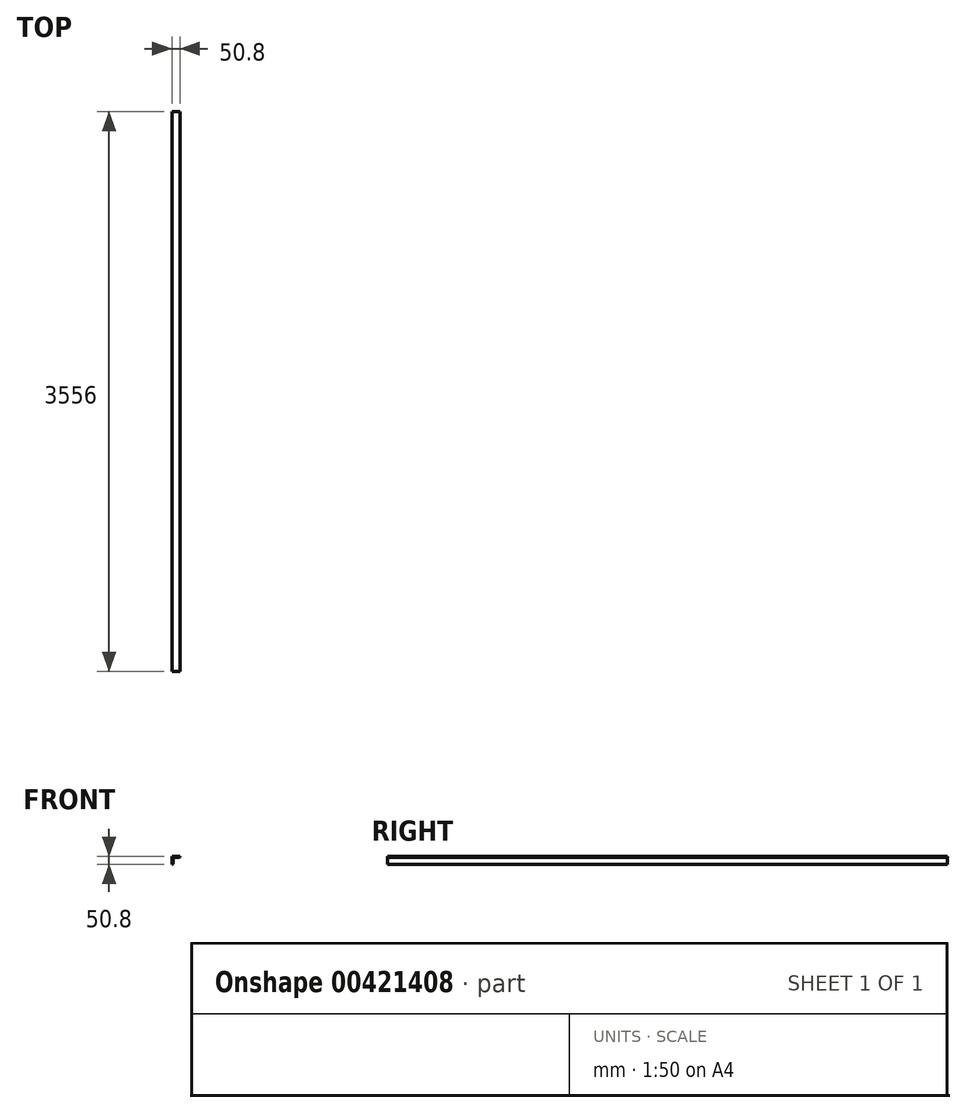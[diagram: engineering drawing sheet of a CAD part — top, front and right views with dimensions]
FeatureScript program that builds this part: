
annotation { "Feature Type Name" : "Feature", "Feature Type Description" : "" }
export const myFeature = defineFeature(function(context is Context, id is Id, definition is map)
    precondition{}
    {
        {
            var Q0;
            Q0=qCreatedBy(makeId("Front.planeOp"),FACE);
            var sketch = newSketch(context, id + "F0", { "sketchPlane" : qUnion([Q0])});
            skLineSegment(sketch, "E0", {"start": v(0, 0) * mm, "end": v(0, 50.8) * mm});
            skLineSegment(sketch, "E1", {"start": v(0, 50.8) * mm, "end": v(50.8, 50.8) * mm});
            skLineSegment(sketch, "E2", {"start": v(50.8, 50.8) * mm, "end": v(50.8, 44.45) * mm});
            skLineSegment(sketch, "E3", {"start": v(50.8, 44.45) * mm, "end": v(6.35, 44.45) * mm});
            skLineSegment(sketch, "E4", {"start": v(6.35, 44.45) * mm, "end": v(6.35, 0) * mm});
            skLineSegment(sketch, "E5", {"start": v(6.35, 0) * mm, "end": v(0, 0) * mm});
            skSolve(sketch);
        }
        {
            var Q0;
            Q0 = qSketchRegion(id + "F0", true);
            extrude(context, id + "F1", {"entities" : qUnion([Q0]), "depth" : 3556 * mm});
        }
        {
            var Q0;
            Q0=makeQuery(id+"F1.opExtrude","SWEPT_EDGE",EDGE,{"disambiguationData":[OSD([sQuery(id+"F0.wireOp",EDGE,"E4"),sQuery(id+"F0.wireOp",EDGE,"E5")])]});
            var Q1;
            Q1=makeQuery(id+"F1.opExtrude","SWEPT_EDGE",EDGE,{"disambiguationData":[OSD([sQuery(id+"F0.wireOp",EDGE,"E2"),sQuery(id+"F0.wireOp",EDGE,"E3")])]});
            var Q2;
            Q2=makeQuery(id+"F1.opExtrude","SWEPT_EDGE",EDGE,{"disambiguationData":[OSD([sQuery(id+"F0.wireOp",EDGE,"E3"),sQuery(id+"F0.wireOp",EDGE,"E4")])]});
            fillet(context, id + "F2", {"entities" : qUnion([Q0, Q1, Q2]), "radius" : 5.08 * mm, "tangentPropagation" : true, "allowEdgeOverflow" : false});
        }
    });
